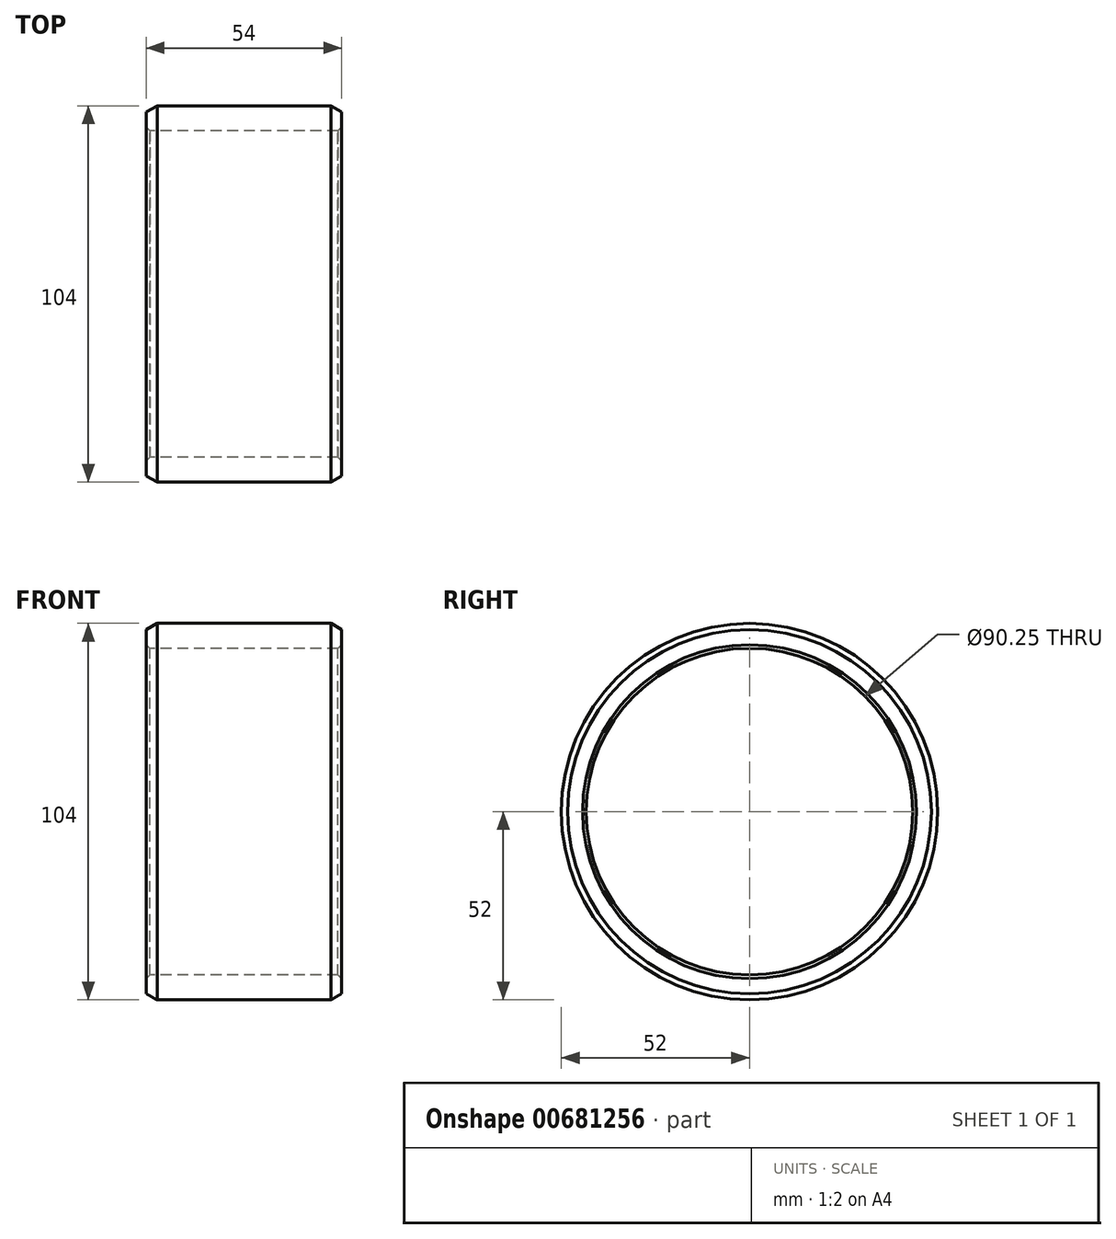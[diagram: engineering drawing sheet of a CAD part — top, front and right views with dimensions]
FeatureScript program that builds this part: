
annotation { "Feature Type Name" : "Feature", "Feature Type Description" : "" }
export const myFeature = defineFeature(function(context is Context, id is Id, definition is map)
    precondition{}
    {
        {
            var Q0;
            Q0=qCreatedBy(makeId("Right.planeOp"),FACE);
            var sketch = newSketch(context, id + "F0", { "sketchPlane" : qUnion([Q0])});
            skCircle(sketch, "E0", {"center": v(0, 0) * mm, "radius": 45.12 * mm});
            skCircle(sketch, "E1", {"center": v(0, 0) * mm, "radius": 52 * mm});
            skSolve(sketch);
        }
        {
            var Q0;
            Q0=qSketchRegion(id+"F0",true);
            extrude(context, id + "F1", {"entities" : qUnion([Q0]), "endBound" : BoundingType.SYMMETRIC, "depth" : 54 * mm, "offsetDistance" : 25 * mm});
        }
        {
            var Q0;
            Q0=makeQuery(id+"F1.opExtrude","CAP_EDGE",EDGE,{"disambiguationData":[OSD([sQuery(id+"F0.wireOp",EDGE,"E0")])],"isStart":false});
            var Q1;
            Q1=makeQuery(id+"F1.opExtrude","CAP_EDGE",EDGE,{"disambiguationData":[OSD([sQuery(id+"F0.wireOp",EDGE,"E0")])],"isStart":true});
            chamfer(context, id + "F2", {"entities" : qUnion([Q0, Q1]), "width" : 1 * mm, "tangentPropagation" : true});
        }
        {
            var Q0;
            Q0=makeQuery(id+"F1.opExtrude","CAP_EDGE",EDGE,{"disambiguationData":[OSD([sQuery(id+"F0.wireOp",EDGE,"E1")])],"isStart":true});
            var Q1;
            Q1=makeQuery(id+"F1.opExtrude","CAP_EDGE",EDGE,{"disambiguationData":[OSD([sQuery(id+"F0.wireOp",EDGE,"E1")])],"isStart":false});
            chamfer(context, id + "F3", {"entities" : qUnion([Q0, Q1]), "chamferType" : ChamferType.OFFSET_ANGLE, "width" : 3 * mm, "oppositeDirection" : false, "angle" : 30 * degree, "tangentPropagation" : true});
        }
    });
